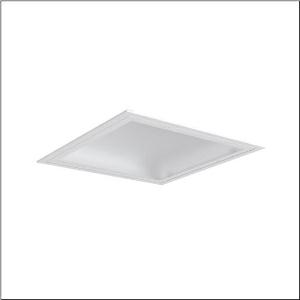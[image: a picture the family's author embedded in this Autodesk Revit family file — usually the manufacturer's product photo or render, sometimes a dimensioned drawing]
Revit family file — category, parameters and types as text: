
# Revit family: mira_r__21_51fr427a442a_c8f5
name_source: partatom
category: Lighting Fixtures
units: mm (PartAtom-declared; Revit-internal decimal feet)

## family parameters
Cut with Voids When Loaded = No
Host = Face
Light Source = No
Part Type = Normal
Room Calculation Point = No
Round Connector Dimension = Use Diameter
Shared = No

## types (1)
- Mira® 21 (1 x LED, 4860 lm, 37 W, 4000K)
    Apparent Load = 37 VA
    CIE Flux Codes = 50 81 97 100 100
    Color Rendering = 80
    Color Temperature = 4000K
    Default Elevation = 1800 mm
    Description = Mira® 21, clean room luminaire, primary light control with reflector, primary optical cover: cover, of PC, light emission: direct distribution, primary light characteristic: symmetric, installation type: recessed, LED, rated luminous flux: 4.860lm, luminous efficacy: 131lm/W, light colour: 840, colour temperature: 4000K, control gear: ECG, with terminal, 3-pole, max. 2.5mm², mains connection: 230V, AC, 50/60Hz, rated input power: 37W, luminaire housing, of sheet steel, coated, pure white (RAL 9010), with concealed spring brackets, module: M625, length: 623mm, width: 623mm, height: 115mm, protection rating (complete): IP54, insulation class (complete): insulation class I (protective earthing), certification: CE, UKCA, permissible operating ambient temperature: -5..+40°C, standard: EN 50419, packaging unit: 1 piece
    Height = 0 mm  [stored 0 ft]
    Lamp = 1 x LED
    Lamp Light Flux = 4860 lm
    Lamp Power = 37 W
    Lamp count = 1
    Length = 625 mm
    Luminous efficacy = 131 lm/W
    Manufacturer = Siteco
    ModVariant = No
    Model = 51FR427A442A
    Mounting Place = Ceiling
    Mounting Type = Recessed
    Number of Poles = 1
    OnlyDefault = Yes
    Power Factor = 1
    Product Name = Mira® 21
    Product group = clean room luminaire
    ProductGroupID = 402
    Protection Class = Protection class I
    Protection Degree = IP 54
    RLX_Detail_Level = 1
    RLX_Emergency_Light_Flux = 0 lm
    RLX_Emergency_Type = 0
    RLX_Emergency_Type_DB = No
    RlxData = <blob elided: 13377 chars, md5=01e7eb7f>
    Socket = socket
    Standby Power = 0 W
    System Light Flux = 4860 lm
    System Power = 37 W
    Type Comments = Product without accessories
    Type Image = l_1007109.jpg
    URL = http://relux.com
    VarID = ---
    Voltage = 0 V
    Weight = 0.00 kg
    Width = 625 mm

note: [stored X ft] marks values corroborated as IEEE doubles in the binary element streams (Revit-internal decimal feet)

## geometry (parser evidence)
native form markers: Sweep x8
no freeform markers — native parametric forms only
